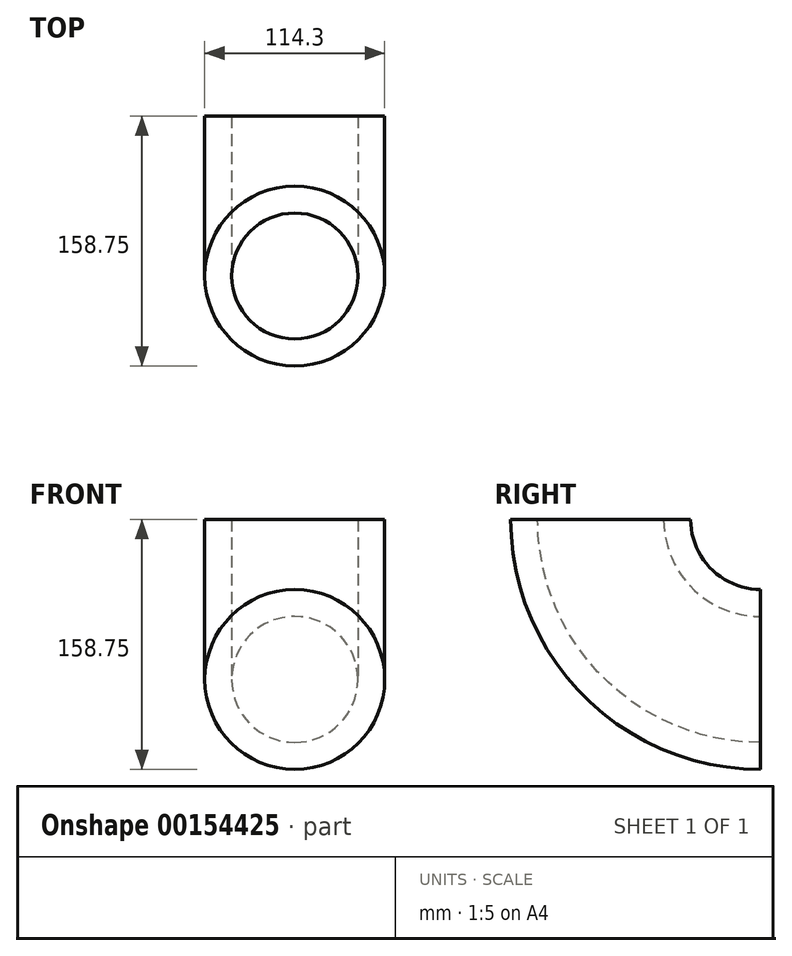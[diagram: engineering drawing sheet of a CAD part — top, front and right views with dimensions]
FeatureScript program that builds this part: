
annotation { "Feature Type Name" : "Feature", "Feature Type Description" : "" }
export const myFeature = defineFeature(function(context is Context, id is Id, definition is map)
    precondition{}
    {
        {
            var Q0;
            Q0=qCreatedBy(makeId("Front.planeOp"),FACE);
            var sketch = newSketch(context, id + "F0", { "sketchPlane" : qUnion([Q0])});
            skCircle(sketch, "E0", {"center": v(0, 0) * mm, "radius": 57.15 * mm});
            skCircle(sketch, "E1.0", {"center": v(0, 0) * mm, "radius": 40.03 * mm});
            skSolve(sketch);
        }
        {
            var Q0;
            Q0=qCreatedBy(makeId("Right.planeOp"),FACE);
            var sketch = newSketch(context, id + "F1", { "sketchPlane" : qUnion([Q0])});
            skLineSegment(sketch, "E2", {"start": v(0, 0) * mm, "end": v(0, 0) * mm});
            skLineSegment(sketch, "E3", {"start": v(-101.6, 101.6) * mm, "end": v(-101.6, 101.6) * mm});
            skPoint(sketch, "E4.visualSharp", {"position": v(-101.6, 0) * mm});
            skArc(sketch, "E4.filletArc", {"start": v(-101.6, 101.6) * mm, "mid": v(-71.84, 29.76) * mm, "end": v(0, 0) * mm});
            skSolve(sketch);
        }
        {
            var Q0;
            Q0=makeQuery(id+"F0.imprint","IMPRINT",FACE,{"disambiguationData":[TD([[makeQuery(id+"F0.imprint","IMPRINT",EDGE,{"derivedFrom":sQuery(id+"F0.wireOp",EDGE,"E0")}),1.0]])]});
            var Q1;
            Q1 = qConstructionFilter(qBodyType(qCreatedBy(id + "F1" ,EDGE), BodyType.WIRE), ConstructionObject.NO);
            sweep(context, id + "F2", {"profiles" : qUnion([Q0]), "path" : qUnion([Q1])});
        }
    });
